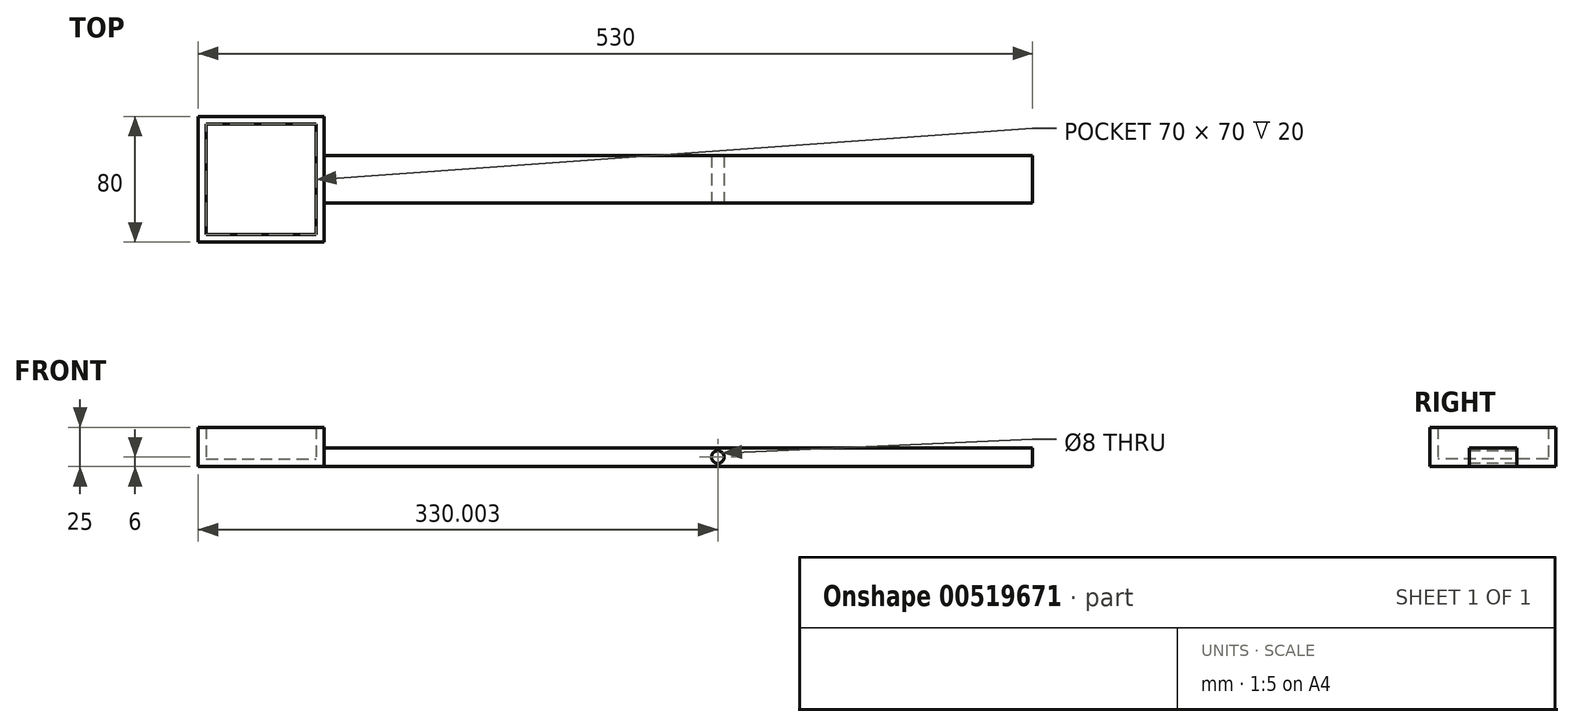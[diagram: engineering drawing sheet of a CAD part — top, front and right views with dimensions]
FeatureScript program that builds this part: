
annotation { "Feature Type Name" : "Feature", "Feature Type Description" : "" }
export const myFeature = defineFeature(function(context is Context, id is Id, definition is map)
    precondition{}
    {
        {
            var Q0;
            Q0=qCreatedBy(makeId("Top.planeOp"),FACE);
            var sketch = newSketch(context, id + "F0", { "sketchPlane" : qUnion([Q0])});
            skLineSegment(sketch, "E0.bottom", {"start": v(-143.03, 29.36) * mm, "end": v(-63.03, 29.36) * mm});
            skLineSegment(sketch, "E0.top", {"start": v(-143.03, -50.64) * mm, "end": v(-63.03, -50.64) * mm});
            skLineSegment(sketch, "E0.left", {"start": v(-143.03, 29.36) * mm, "end": v(-143.03, -50.64) * mm});
            skLineSegment(sketch, "E0.right", {"start": v(-63.03, 29.36) * mm, "end": v(-63.03, -50.64) * mm});
            skLineSegment(sketch, "E1.bottom", {"start": v(-63.03, 4.36) * mm, "end": v(386.97, 4.36) * mm});
            skLineSegment(sketch, "E1.top", {"start": v(-63.03, -25.64) * mm, "end": v(386.97, -25.64) * mm});
            skLineSegment(sketch, "E1.left", {"start": v(-63.03, 4.36) * mm, "end": v(-63.03, -25.64) * mm});
            skLineSegment(sketch, "E1.right", {"start": v(386.97, 4.36) * mm, "end": v(386.97, -25.64) * mm});
            skLineSegment(sketch, "E2.bottom", {"start": v(-138.03, 24.36) * mm, "end": v(-68.03, 24.36) * mm});
            skLineSegment(sketch, "E2.top", {"start": v(-138.03, -45.64) * mm, "end": v(-68.03, -45.64) * mm});
            skLineSegment(sketch, "E2.left", {"start": v(-138.03, 24.36) * mm, "end": v(-138.03, -45.64) * mm});
            skLineSegment(sketch, "E2.right", {"start": v(-68.03, 24.36) * mm, "end": v(-68.03, -45.64) * mm});
            skSolve(sketch);
        }
        {
            var Q0;
            Q0=makeQuery(id+"F0.imprint","IMPRINT",FACE,{"disambiguationData":[TD([[makeQuery(id+"F0.imprint","IMPRINT",EDGE,{"derivedFrom":sQuery(id+"F0.wireOp",EDGE,"E1.bottom")}),-1.0]])]});
            extrude(context, id + "F1", {"entities" : qUnion([Q0]), "depth" : 12 * mm, "offsetDistance" : 25 * mm});
        }
        {
            var Q0;
            {var subQ1=sQuery(id+"F0.wireOp",EDGE,"E0.bottom");Q0=makeQuery(id+"F0.imprint","IMPRINT",FACE,{"disambiguationData":[TD([[makeQuery(id+"F0.imprint","IMPRINT",EDGE,{"derivedFrom":subQ1}),-1.0]])]});}
            extrude(context, id + "F2", {"entities" : qUnion([Q0]), "operationType" : NewBodyOperationType.ADD, "depth" : 25 * mm, "offsetDistance" : 25 * mm});
        }
        {
            var Q0;
            Q0=makeQuery(id+"F0.imprint","IMPRINT",FACE,{"disambiguationData":[TD([[makeQuery(id+"F0.imprint","IMPRINT",EDGE,{"derivedFrom":sQuery(id+"F0.wireOp",EDGE,"E2.bottom")}),-1.0]])]});
            extrude(context, id + "F3", {"entities" : qUnion([Q0]), "operationType" : NewBodyOperationType.ADD, "depth" : 5 * mm, "offsetDistance" : 25 * mm});
        }
        {
            var Q0;
            Q0=makeQuery(id+"F1.opExtrude","SWEPT_FACE",FACE,{"disambiguationData":[OSD([sQuery(id+"F0.wireOp",EDGE,"E1.top")])]});
            var sketch = newSketch(context, id + "F4", { "sketchPlane" : qUnion([Q0])});
            skCircle(sketch, "E3", {"center": v(186.97, 6) * mm, "radius": 4 * mm});
            skSolve(sketch);
        }
        {
            var Q0;
            Q0=sQuery(id+"F4.wireOp",VERTEX,"E3.center");
            var Q1;
            Q1=makeQuery(id+"F1.opExtrude","SWEPT_BODY",BODY,{"disambiguationData":[OSD([sQuery(id+"F0.wireOp",EDGE,"E1.bottom"),sQuery(id+"F0.wireOp",EDGE,"E1.top"),sQuery(id+"F0.wireOp",EDGE,"E1.left"),sQuery(id+"F0.wireOp",EDGE,"E1.right")])]});
            hole(context, id + "F5", {"style" : HoleStyle.SIMPLE, "endStyle" : HoleEndStyle.THROUGH, "holeDiameter" : 8 * mm, "isTappedThrough" : true, "tappedDepth" : 12 * mm, "tapClearance" : 3, "locations" : qUnion([Q0]), "scope" : qUnion([Q1])});
        }
    });
